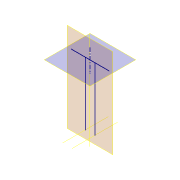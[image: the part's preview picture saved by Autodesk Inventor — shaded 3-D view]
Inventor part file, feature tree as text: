
AUTODESK INVENTOR PART (.ipt)
format: ipt  version: 2016 (Build 200138000, 138)  size: 70,656 bytes
history: native  units: in
note: dims shown in document units (in); Inventor stores cm internally (conversion verified against a paired STEP export)
features: other x7, plane x2, sketch x1
ambient origin geometry x8: Origin, YZ Plane, XZ Plane, XY Plane, X Axis, Y Axis, Z Axis, Center Point
feature tree (10):
  other  "skeleton.ipt"
  other  "Blocks"
  plane  "Work Plane6"
  other  "Work Axis5"
  other  "Work Axis6"
  plane  "Work Plane7"
  other  "Work Axis7"
  other  "L1_legs"
  sketch  "Sketch1"  dims[d7=0.3937in d0=2.3622in d1=11.811in d2=9.4488in d5=1.9291in d6=5.9055in d12=1.9291in d13=1.5748in d8=90.0deg]
  other  "L1_legs:1"
